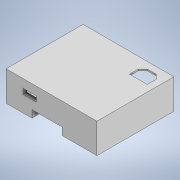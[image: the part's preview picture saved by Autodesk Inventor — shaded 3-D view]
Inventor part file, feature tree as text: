
AUTODESK INVENTOR PART (.ipt)
format: ipt  version: 2022 (Build 260153000, 153)  size: 276,992 bytes
history: native  units: in
note: dims shown in document units (in); Inventor stores cm internally (conversion verified against a paired STEP export)
features: extrude x11, sketch x10
ambient origin geometry x8: Origin, YZ Plane, XZ Plane, XY Plane, X Axis, Y Axis, Z Axis, Center Point
bodies: Solid1 (feature_tree)
feature tree (21):
  sketch  "Sketch1"  dims[d0=2.2047in d1=1.9685in]
  extrude  "Extrusion1"  Depth=1.9685in
  extrude  "Extrusion2"  Depth=0.0079in
  extrude  "Extrusion3"  TaperAngle=0.0deg  [1 undecoded]
  extrude  "Extrusion5"  Depth=0.0984in
  extrude  "Extrusion6"  Depth=0.0984in
  extrude  "Extrusion7"  Depth=0.0394in TaperAngle=0.0deg
  extrude  "Extrusion8"  Depth=0.0984in
  extrude  "Extrusion9"  Depth=0.0394in
  extrude  "Extrusion10"  TaperAngle=0.0deg  [1 undecoded]
  extrude  "Extrusion11"  Depth=0.0394in
  extrude  "Extrusion12"  Depth=0.0984in
  sketch  "Sketch2"  dims[d2=0.0079in d3=0.0079in]
  sketch  "Sketch3"  dims[d4=0.0in d5=0.0in]
  sketch  "Sketch4"  dims[d6=0.0984in d7=0.0984in]
  sketch  "Sketch5"  dims[d8=0.0984in d9=0.0984in]
  sketch  "Sketch6"  dims[d10=0.5984in d11=0.0in d12=0.0394in d13=0.0in]
  sketch  "Sketch7"  dims[d14=0.0in d16=0.0984in]
  sketch  "Sketch8"  dims[d17=0.0394in d18=0.0394in]
  sketch  "Sketch9"  dims[d19=0.0in d20=0.0in]
  sketch  "Sketch10"  dims[d21=0.0669in d22=0.0394in d23=0.0984in d24=0.0in d25=0.5906in d26=0.8268in d27=0.0in d30=0.1969in d31=2.9813in d32=0.0in d33=0.2953in d34=0.4331in d35=0.7087in d36=0.3543in d37=2.9813in d38=0.0in d39=0.1181in d40=0.0in d41=1.4173in d42=1.6535in d43=0.0787in d44=0.5512in d45=0.1181in d46=0.1181in d47=45.0deg d48=135.0deg d49=0.1181in d50=0.0394in d51=0.0in d52=0.0394in d53=0.0394in d54=0.0394in d55=0.0394in d56=0.3937in d57=0.0in d58=0.1181in d59=0.3937in d60=0.0in d61=0.0394in d62=0.0in d63=0.0394in d64=0.0394in d65=0.0in]
note: 2 required parameter values undecoded (feature->parameter linkage not recoverable at this tier; creation-order binding heuristic only, values carry confidence <= 0.55)
